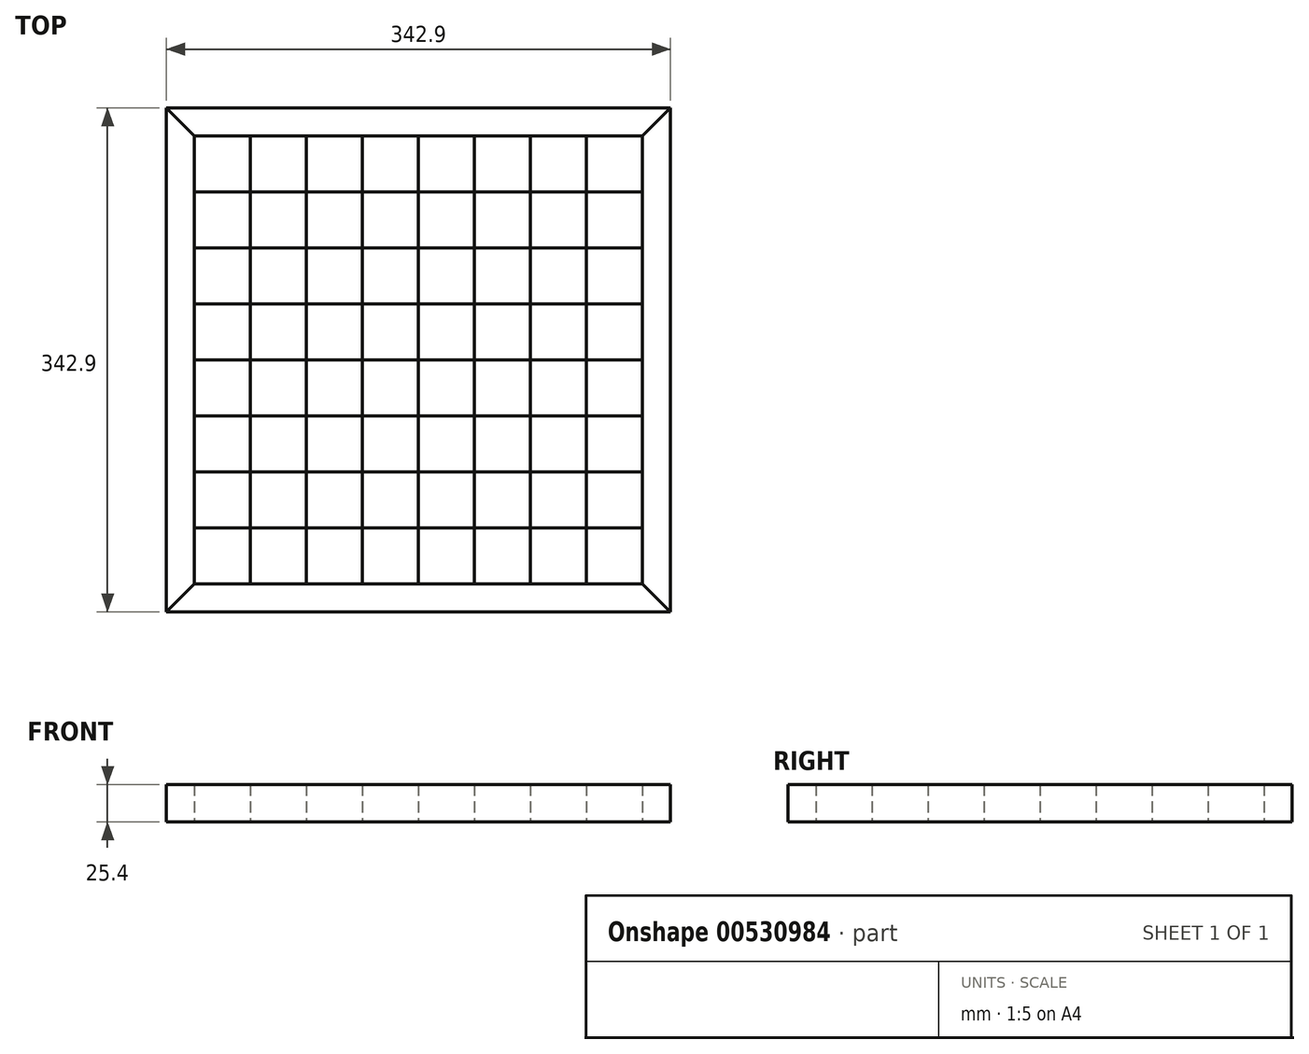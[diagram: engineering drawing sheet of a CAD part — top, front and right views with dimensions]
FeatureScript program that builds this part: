
annotation { "Feature Type Name" : "Feature", "Feature Type Description" : "" }
export const myFeature = defineFeature(function(context is Context, id is Id, definition is map)
    precondition{}
    {
        {
            var Q0;
            Q0=qCreatedBy(makeId("Top.planeOp"),FACE);
            var sketch = newSketch(context, id + "F0", { "sketchPlane" : qUnion([Q0])});
            skLineSegment(sketch, "E0.bottom", {"start": v(171.45, 171.45) * mm, "end": v(-171.45, 171.45) * mm});
            skLineSegment(sketch, "E0.top", {"start": v(171.45, -171.45) * mm, "end": v(-171.45, -171.45) * mm});
            skLineSegment(sketch, "E0.left", {"start": v(171.45, 171.45) * mm, "end": v(171.45, -171.45) * mm});
            skLineSegment(sketch, "E0.right", {"start": v(-171.45, 171.45) * mm, "end": v(-171.45, -171.45) * mm});
            skPoint(sketch, "E0.middle", {"position": v(0, 0) * mm});
            skLineSegment(sketch, "E1.bottom", {"start": v(152.4, 152.4) * mm, "end": v(-152.4, 152.4) * mm});
            skLineSegment(sketch, "E1.top", {"start": v(152.4, -152.4) * mm, "end": v(-152.4, -152.4) * mm});
            skLineSegment(sketch, "E1.left", {"start": v(152.4, 152.4) * mm, "end": v(152.4, -152.4) * mm});
            skLineSegment(sketch, "E1.right", {"start": v(-152.4, 152.4) * mm, "end": v(-152.4, -152.4) * mm});
            skLineSegment(sketch, "E2", {"start": v(152.4, 152.4) * mm, "end": v(171.45, 171.45) * mm});
            skLineSegment(sketch, "E3", {"start": v(152.4, -152.4) * mm, "end": v(171.45, -171.45) * mm});
            skLineSegment(sketch, "E4", {"start": v(-152.4, -152.4) * mm, "end": v(-171.45, -171.45) * mm});
            skLineSegment(sketch, "E5", {"start": v(-152.4, 152.4) * mm, "end": v(-171.45, 171.45) * mm});
            skLineSegment(sketch, "E6", {"start": v(-114.3, 152.4) * mm, "end": v(-114.3, -152.4) * mm});
            skLineSegment(sketch, "E7", {"start": v(-76.2, 152.4) * mm, "end": v(-76.2, -152.4) * mm});
            skLineSegment(sketch, "E8", {"start": v(-38.1, 152.4) * mm, "end": v(-38.1, -152.4) * mm});
            skLineSegment(sketch, "E9", {"start": v(0, -152.4) * mm, "end": v(0, 152.4) * mm});
            skLineSegment(sketch, "E10", {"start": v(38.1, 152.4) * mm, "end": v(38.1, -152.4) * mm});
            skLineSegment(sketch, "E11", {"start": v(76.2, 152.4) * mm, "end": v(76.2, -152.4) * mm});
            skLineSegment(sketch, "E12", {"start": v(114.3, 152.4) * mm, "end": v(114.3, -152.4) * mm});
            skLineSegment(sketch, "E13", {"start": v(-152.4, 0) * mm, "end": v(152.4, 0) * mm});
            skLineSegment(sketch, "E14", {"start": v(-152.4, 38.1) * mm, "end": v(152.4, 38.1) * mm});
            skLineSegment(sketch, "E15", {"start": v(-152.4, 76.2) * mm, "end": v(152.4, 76.2) * mm});
            skLineSegment(sketch, "E16", {"start": v(-152.4, 114.3) * mm, "end": v(152.4, 114.3) * mm});
            skLineSegment(sketch, "E17", {"start": v(-152.4, -38.1) * mm, "end": v(152.4, -38.1) * mm});
            skLineSegment(sketch, "E18", {"start": v(-152.4, -76.2) * mm, "end": v(152.4, -76.2) * mm});
            skLineSegment(sketch, "E19", {"start": v(-152.4, -114.3) * mm, "end": v(152.4, -114.3) * mm});
            skSolve(sketch);
        }
        {
            var Q0;
            Q0=makeQuery(id+"F0.imprint","IMPRINT",FACE,{"disambiguationData":[TD([[makeQuery(id+"F0.imprint","IMPRINT",EDGE,{"derivedFrom":sQuery(id+"F0.wireOp",EDGE,"E0.right")}),1.0]])]});
            extrude(context, id + "F1", {"entities" : qUnion([Q0]), "depth" : 25.4 * mm, "offsetDistance" : 25.4 * mm});
        }
        {
            var Q0;
            Q0=makeQuery(id+"F0.imprint","IMPRINT",FACE,{"disambiguationData":[TD([[makeQuery(id+"F0.imprint","IMPRINT",EDGE,{"derivedFrom":sQuery(id+"F0.wireOp",EDGE,"E0.bottom")}),1.0]])]});
            extrude(context, id + "F2", {"entities" : qUnion([Q0]), "depth" : 25.4 * mm, "offsetDistance" : 25.4 * mm});
        }
        {
            var Q0;
            Q0=makeQuery(id+"F0.imprint","IMPRINT",FACE,{"disambiguationData":[TD([[makeQuery(id+"F0.imprint","IMPRINT",EDGE,{"derivedFrom":sQuery(id+"F0.wireOp",EDGE,"E0.left")}),-1.0]])]});
            extrude(context, id + "F3", {"entities" : qUnion([Q0]), "depth" : 25.4 * mm, "offsetDistance" : 25.4 * mm});
        }
        {
            var Q0;
            Q0=makeQuery(id+"F0.imprint","IMPRINT",FACE,{"disambiguationData":[TD([[makeQuery(id+"F0.imprint","IMPRINT",EDGE,{"derivedFrom":sQuery(id+"F0.wireOp",EDGE,"E0.top")}),-1.0]])]});
            extrude(context, id + "F4", {"entities" : qUnion([Q0]), "depth" : 25.4 * mm, "offsetDistance" : 25.4 * mm});
        }
        {
            var Q0;
            {var subQ1=sQuery(id+"F0.wireOp",EDGE,"E1.bottom");var subQ3=sQuery(id+"F0.wireOp",EDGE,"E6");var subQ4=makeQuery(id+"F0.imprint","INTERSECT",VERTEX,{"derivedFrom":[subQ1,subQ3]});Q0=makeQuery(id+"F0.imprint","IMPRINT",FACE,{"disambiguationData":[TD([[makeQuery(id+"F0.imprint","IMPRINT",EDGE,{"disambiguationData":[TD([[subQ4,-1.0]])],"derivedFrom":subQ3}),-1.0]])]});}
            var Q1;
            {var subQ0=sQuery(id+"F0.wireOp",EDGE,"E16");var subQ1=sQuery(id+"F0.wireOp",EDGE,"E6");var subQ2=makeQuery(id+"F0.imprint","INTERSECT",VERTEX,{"derivedFrom":[subQ1,subQ0]});Q1=makeQuery(id+"F0.imprint","IMPRINT",FACE,{"disambiguationData":[TD([[makeQuery(id+"F0.imprint","IMPRINT",EDGE,{"disambiguationData":[TD([[subQ2,-1.0]])],"derivedFrom":subQ1}),1.0]])]});}
            var Q2;
            {var subQ0=sQuery(id+"F0.wireOp",EDGE,"E7");var subQ1=sQuery(id+"F0.wireOp",EDGE,"E1.bottom");var subQ2=makeQuery(id+"F0.imprint","INTERSECT",VERTEX,{"derivedFrom":[subQ1,subQ0]});Q2=makeQuery(id+"F0.imprint","IMPRINT",FACE,{"disambiguationData":[TD([[makeQuery(id+"F0.imprint","IMPRINT",EDGE,{"disambiguationData":[TD([[subQ2,1.0]])],"derivedFrom":subQ1}),1.0]])]});}
            var Q3;
            {var subQ0=sQuery(id+"F0.wireOp",EDGE,"E16");var subQ1=sQuery(id+"F0.wireOp",EDGE,"E8");var subQ2=makeQuery(id+"F0.imprint","INTERSECT",VERTEX,{"derivedFrom":[subQ1,subQ0]});Q3=makeQuery(id+"F0.imprint","IMPRINT",FACE,{"disambiguationData":[TD([[makeQuery(id+"F0.imprint","IMPRINT",EDGE,{"disambiguationData":[TD([[subQ2,-1.0]])],"derivedFrom":subQ1}),1.0]])]});}
            var Q4;
            {var subQ0=sQuery(id+"F0.wireOp",EDGE,"E9");var subQ1=sQuery(id+"F0.wireOp",EDGE,"E1.bottom");var subQ2=makeQuery(id+"F0.imprint","INTERSECT",VERTEX,{"derivedFrom":[subQ1,subQ0]});Q4=makeQuery(id+"F0.imprint","IMPRINT",FACE,{"disambiguationData":[TD([[makeQuery(id+"F0.imprint","IMPRINT",EDGE,{"disambiguationData":[TD([[subQ2,1.0]])],"derivedFrom":subQ1}),1.0]])]});}
            var Q5;
            {var subQ0=sQuery(id+"F0.wireOp",EDGE,"E16");var subQ1=sQuery(id+"F0.wireOp",EDGE,"E10");var subQ2=makeQuery(id+"F0.imprint","INTERSECT",VERTEX,{"derivedFrom":[subQ1,subQ0]});Q5=makeQuery(id+"F0.imprint","IMPRINT",FACE,{"disambiguationData":[TD([[makeQuery(id+"F0.imprint","IMPRINT",EDGE,{"disambiguationData":[TD([[subQ2,-1.0]])],"derivedFrom":subQ1}),1.0]])]});}
            var Q6;
            {var subQ0=sQuery(id+"F0.wireOp",EDGE,"E11");var subQ1=sQuery(id+"F0.wireOp",EDGE,"E1.bottom");var subQ2=makeQuery(id+"F0.imprint","INTERSECT",VERTEX,{"derivedFrom":[subQ1,subQ0]});Q6=makeQuery(id+"F0.imprint","IMPRINT",FACE,{"disambiguationData":[TD([[makeQuery(id+"F0.imprint","IMPRINT",EDGE,{"disambiguationData":[TD([[subQ2,1.0]])],"derivedFrom":subQ1}),1.0]])]});}
            var Q7;
            {var subQ0=sQuery(id+"F0.wireOp",EDGE,"E15");var subQ1=sQuery(id+"F0.wireOp",EDGE,"E1.left");var subQ2=makeQuery(id+"F0.imprint","INTERSECT",VERTEX,{"derivedFrom":[subQ1,subQ0]});Q7=makeQuery(id+"F0.imprint","IMPRINT",FACE,{"disambiguationData":[TD([[makeQuery(id+"F0.imprint","IMPRINT",EDGE,{"disambiguationData":[TD([[subQ2,1.0]])],"derivedFrom":subQ1}),-1.0]])]});}
            var Q8;
            {var subQ0=sQuery(id+"F0.wireOp",EDGE,"E15");var subQ1=sQuery(id+"F0.wireOp",EDGE,"E11");var subQ2=makeQuery(id+"F0.imprint","INTERSECT",VERTEX,{"derivedFrom":[subQ1,subQ0]});Q8=makeQuery(id+"F0.imprint","IMPRINT",FACE,{"disambiguationData":[TD([[makeQuery(id+"F0.imprint","IMPRINT",EDGE,{"disambiguationData":[TD([[subQ2,-1.0]])],"derivedFrom":subQ1}),1.0]])]});}
            var Q9;
            {var subQ0=sQuery(id+"F0.wireOp",EDGE,"E14");var subQ1=sQuery(id+"F0.wireOp",EDGE,"E10");var subQ2=makeQuery(id+"F0.imprint","INTERSECT",VERTEX,{"derivedFrom":[subQ1,subQ0]});Q9=makeQuery(id+"F0.imprint","IMPRINT",FACE,{"disambiguationData":[TD([[makeQuery(id+"F0.imprint","IMPRINT",EDGE,{"disambiguationData":[TD([[subQ2,-1.0]])],"derivedFrom":subQ1}),1.0]])]});}
            var Q10;
            {var subQ0=sQuery(id+"F0.wireOp",EDGE,"E13");var subQ1=sQuery(id+"F0.wireOp",EDGE,"E1.left");var subQ2=makeQuery(id+"F0.imprint","INTERSECT",VERTEX,{"derivedFrom":[subQ1,subQ0]});Q10=makeQuery(id+"F0.imprint","IMPRINT",FACE,{"disambiguationData":[TD([[makeQuery(id+"F0.imprint","IMPRINT",EDGE,{"disambiguationData":[TD([[subQ2,1.0]])],"derivedFrom":subQ1}),-1.0]])]});}
            var Q11;
            {var subQ0=sQuery(id+"F0.wireOp",EDGE,"E14");var subQ1=sQuery(id+"F0.wireOp",EDGE,"E9");var subQ2=makeQuery(id+"F0.imprint","INTERSECT",VERTEX,{"derivedFrom":[subQ1,subQ0]});Q11=makeQuery(id+"F0.imprint","IMPRINT",FACE,{"disambiguationData":[TD([[makeQuery(id+"F0.imprint","IMPRINT",EDGE,{"disambiguationData":[TD([[subQ2,-1.0]])],"derivedFrom":subQ1}),-1.0]])]});}
            var Q12;
            {var subQ0=sQuery(id+"F0.wireOp",EDGE,"E14");var subQ1=sQuery(id+"F0.wireOp",EDGE,"E8");var subQ2=makeQuery(id+"F0.imprint","INTERSECT",VERTEX,{"derivedFrom":[subQ1,subQ0]});Q12=makeQuery(id+"F0.imprint","IMPRINT",FACE,{"disambiguationData":[TD([[makeQuery(id+"F0.imprint","IMPRINT",EDGE,{"disambiguationData":[TD([[subQ2,-1.0]])],"derivedFrom":subQ1}),1.0]])]});}
            var Q13;
            {var subQ0=sQuery(id+"F0.wireOp",EDGE,"E15");var subQ1=sQuery(id+"F0.wireOp",EDGE,"E7");var subQ2=makeQuery(id+"F0.imprint","INTERSECT",VERTEX,{"derivedFrom":[subQ1,subQ0]});Q13=makeQuery(id+"F0.imprint","IMPRINT",FACE,{"disambiguationData":[TD([[makeQuery(id+"F0.imprint","IMPRINT",EDGE,{"disambiguationData":[TD([[subQ2,-1.0]])],"derivedFrom":subQ1}),1.0]])]});}
            var Q14;
            {var subQ0=sQuery(id+"F0.wireOp",EDGE,"E14");var subQ1=sQuery(id+"F0.wireOp",EDGE,"E6");var subQ2=makeQuery(id+"F0.imprint","INTERSECT",VERTEX,{"derivedFrom":[subQ1,subQ0]});Q14=makeQuery(id+"F0.imprint","IMPRINT",FACE,{"disambiguationData":[TD([[makeQuery(id+"F0.imprint","IMPRINT",EDGE,{"disambiguationData":[TD([[subQ2,-1.0]])],"derivedFrom":subQ1}),1.0]])]});}
            var Q15;
            {var subQ0=sQuery(id+"F0.wireOp",EDGE,"E14");var subQ1=sQuery(id+"F0.wireOp",EDGE,"E1.right");var subQ2=makeQuery(id+"F0.imprint","INTERSECT",VERTEX,{"derivedFrom":[subQ1,subQ0]});Q15=makeQuery(id+"F0.imprint","IMPRINT",FACE,{"disambiguationData":[TD([[makeQuery(id+"F0.imprint","IMPRINT",EDGE,{"disambiguationData":[TD([[subQ2,1.0]])],"derivedFrom":subQ1}),1.0]])]});}
            var Q16;
            {var subQ0=sQuery(id+"F0.wireOp",EDGE,"E13");var subQ1=sQuery(id+"F0.wireOp",EDGE,"E1.right");var subQ2=makeQuery(id+"F0.imprint","INTERSECT",VERTEX,{"derivedFrom":[subQ1,subQ0]});Q16=makeQuery(id+"F0.imprint","IMPRINT",FACE,{"disambiguationData":[TD([[makeQuery(id+"F0.imprint","IMPRINT",EDGE,{"disambiguationData":[TD([[subQ2,-1.0]])],"derivedFrom":subQ1}),1.0]])]});}
            var Q17;
            {var subQ0=sQuery(id+"F0.wireOp",EDGE,"E17");var subQ1=sQuery(id+"F0.wireOp",EDGE,"E6");var subQ2=makeQuery(id+"F0.imprint","INTERSECT",VERTEX,{"derivedFrom":[subQ1,subQ0]});Q17=makeQuery(id+"F0.imprint","IMPRINT",FACE,{"disambiguationData":[TD([[makeQuery(id+"F0.imprint","IMPRINT",EDGE,{"disambiguationData":[TD([[subQ2,-1.0]])],"derivedFrom":subQ1}),1.0]])]});}
            var Q18;
            {var subQ0=sQuery(id+"F0.wireOp",EDGE,"E13");var subQ1=sQuery(id+"F0.wireOp",EDGE,"E7");var subQ2=makeQuery(id+"F0.imprint","INTERSECT",VERTEX,{"derivedFrom":[subQ1,subQ0]});Q18=makeQuery(id+"F0.imprint","IMPRINT",FACE,{"disambiguationData":[TD([[makeQuery(id+"F0.imprint","IMPRINT",EDGE,{"disambiguationData":[TD([[subQ2,-1.0]])],"derivedFrom":subQ1}),1.0]])]});}
            var Q19;
            {var subQ0=sQuery(id+"F0.wireOp",EDGE,"E17");var subQ1=sQuery(id+"F0.wireOp",EDGE,"E8");var subQ2=makeQuery(id+"F0.imprint","INTERSECT",VERTEX,{"derivedFrom":[subQ1,subQ0]});Q19=makeQuery(id+"F0.imprint","IMPRINT",FACE,{"disambiguationData":[TD([[makeQuery(id+"F0.imprint","IMPRINT",EDGE,{"disambiguationData":[TD([[subQ2,-1.0]])],"derivedFrom":subQ1}),1.0]])]});}
            var Q20;
            {var subQ0=sQuery(id+"F0.wireOp",EDGE,"E17");var subQ1=sQuery(id+"F0.wireOp",EDGE,"E9");var subQ2=makeQuery(id+"F0.imprint","INTERSECT",VERTEX,{"derivedFrom":[subQ1,subQ0]});Q20=makeQuery(id+"F0.imprint","IMPRINT",FACE,{"disambiguationData":[TD([[makeQuery(id+"F0.imprint","IMPRINT",EDGE,{"disambiguationData":[TD([[subQ2,-1.0]])],"derivedFrom":subQ1}),-1.0]])]});}
            var Q21;
            {var subQ0=sQuery(id+"F0.wireOp",EDGE,"E17");var subQ1=sQuery(id+"F0.wireOp",EDGE,"E10");var subQ2=makeQuery(id+"F0.imprint","INTERSECT",VERTEX,{"derivedFrom":[subQ1,subQ0]});Q21=makeQuery(id+"F0.imprint","IMPRINT",FACE,{"disambiguationData":[TD([[makeQuery(id+"F0.imprint","IMPRINT",EDGE,{"disambiguationData":[TD([[subQ2,-1.0]])],"derivedFrom":subQ1}),1.0]])]});}
            var Q22;
            {var subQ0=sQuery(id+"F0.wireOp",EDGE,"E13");var subQ1=sQuery(id+"F0.wireOp",EDGE,"E11");var subQ2=makeQuery(id+"F0.imprint","INTERSECT",VERTEX,{"derivedFrom":[subQ1,subQ0]});Q22=makeQuery(id+"F0.imprint","IMPRINT",FACE,{"disambiguationData":[TD([[makeQuery(id+"F0.imprint","IMPRINT",EDGE,{"disambiguationData":[TD([[subQ2,-1.0]])],"derivedFrom":subQ1}),1.0]])]});}
            var Q23;
            {var subQ0=sQuery(id+"F0.wireOp",EDGE,"E17");var subQ1=sQuery(id+"F0.wireOp",EDGE,"E1.left");var subQ2=makeQuery(id+"F0.imprint","INTERSECT",VERTEX,{"derivedFrom":[subQ1,subQ0]});Q23=makeQuery(id+"F0.imprint","IMPRINT",FACE,{"disambiguationData":[TD([[makeQuery(id+"F0.imprint","IMPRINT",EDGE,{"disambiguationData":[TD([[subQ2,-1.0]])],"derivedFrom":subQ1}),-1.0]])]});}
            var Q24;
            {var subQ0=sQuery(id+"F0.wireOp",EDGE,"E18");var subQ1=sQuery(id+"F0.wireOp",EDGE,"E11");var subQ2=makeQuery(id+"F0.imprint","INTERSECT",VERTEX,{"derivedFrom":[subQ1,subQ0]});Q24=makeQuery(id+"F0.imprint","IMPRINT",FACE,{"disambiguationData":[TD([[makeQuery(id+"F0.imprint","IMPRINT",EDGE,{"disambiguationData":[TD([[subQ2,-1.0]])],"derivedFrom":subQ1}),1.0]])]});}
            var Q25;
            {var subQ0=sQuery(id+"F0.wireOp",EDGE,"E19");var subQ1=sQuery(id+"F0.wireOp",EDGE,"E9");var subQ2=makeQuery(id+"F0.imprint","INTERSECT",VERTEX,{"derivedFrom":[subQ1,subQ0]});Q25=makeQuery(id+"F0.imprint","IMPRINT",FACE,{"disambiguationData":[TD([[makeQuery(id+"F0.imprint","IMPRINT",EDGE,{"disambiguationData":[TD([[subQ2,-1.0]])],"derivedFrom":subQ1}),-1.0]])]});}
            var Q26;
            {var subQ0=sQuery(id+"F0.wireOp",EDGE,"E18");var subQ1=sQuery(id+"F0.wireOp",EDGE,"E7");var subQ2=makeQuery(id+"F0.imprint","INTERSECT",VERTEX,{"derivedFrom":[subQ1,subQ0]});Q26=makeQuery(id+"F0.imprint","IMPRINT",FACE,{"disambiguationData":[TD([[makeQuery(id+"F0.imprint","IMPRINT",EDGE,{"disambiguationData":[TD([[subQ2,-1.0]])],"derivedFrom":subQ1}),1.0]])]});}
            var Q27;
            {var subQ0=sQuery(id+"F0.wireOp",EDGE,"E18");var subQ1=sQuery(id+"F0.wireOp",EDGE,"E1.right");var subQ2=makeQuery(id+"F0.imprint","INTERSECT",VERTEX,{"derivedFrom":[subQ1,subQ0]});Q27=makeQuery(id+"F0.imprint","IMPRINT",FACE,{"disambiguationData":[TD([[makeQuery(id+"F0.imprint","IMPRINT",EDGE,{"disambiguationData":[TD([[subQ2,-1.0]])],"derivedFrom":subQ1}),1.0]])]});}
            var Q28;
            {var subQ0=sQuery(id+"F0.wireOp",EDGE,"E6");var subQ1=sQuery(id+"F0.wireOp",EDGE,"E1.top");var subQ2=makeQuery(id+"F0.imprint","INTERSECT",VERTEX,{"derivedFrom":[subQ1,subQ0]});Q28=makeQuery(id+"F0.imprint","IMPRINT",FACE,{"disambiguationData":[TD([[makeQuery(id+"F0.imprint","IMPRINT",EDGE,{"disambiguationData":[TD([[subQ2,1.0]])],"derivedFrom":subQ1}),-1.0]])]});}
            var Q29;
            {var subQ0=sQuery(id+"F0.wireOp",EDGE,"E8");var subQ1=sQuery(id+"F0.wireOp",EDGE,"E1.top");var subQ2=makeQuery(id+"F0.imprint","INTERSECT",VERTEX,{"derivedFrom":[subQ1,subQ0]});Q29=makeQuery(id+"F0.imprint","IMPRINT",FACE,{"disambiguationData":[TD([[makeQuery(id+"F0.imprint","IMPRINT",EDGE,{"disambiguationData":[TD([[subQ2,1.0]])],"derivedFrom":subQ1}),-1.0]])]});}
            var Q30;
            {var subQ0=sQuery(id+"F0.wireOp",EDGE,"E10");var subQ1=sQuery(id+"F0.wireOp",EDGE,"E1.top");var subQ2=makeQuery(id+"F0.imprint","INTERSECT",VERTEX,{"derivedFrom":[subQ1,subQ0]});Q30=makeQuery(id+"F0.imprint","IMPRINT",FACE,{"disambiguationData":[TD([[makeQuery(id+"F0.imprint","IMPRINT",EDGE,{"disambiguationData":[TD([[subQ2,1.0]])],"derivedFrom":subQ1}),-1.0]])]});}
            var Q31;
            {var subQ1=sQuery(id+"F0.wireOp",EDGE,"E1.top");var subQ3=sQuery(id+"F0.wireOp",EDGE,"E12");var subQ4=makeQuery(id+"F0.imprint","INTERSECT",VERTEX,{"derivedFrom":[subQ1,subQ3]});Q31=makeQuery(id+"F0.imprint","IMPRINT",FACE,{"disambiguationData":[TD([[makeQuery(id+"F0.imprint","IMPRINT",EDGE,{"disambiguationData":[TD([[subQ4,1.0]])],"derivedFrom":subQ3}),1.0]])]});}
            extrude(context, id + "F5", {"entities" : qUnion([Q0, Q1, Q2, Q3, Q4, Q5, Q6, Q7, Q8, Q9, Q10, Q11, Q12, Q13, Q14, Q15, Q16, Q17, Q18, Q19, Q20, Q21, Q22, Q23, Q24, Q25, Q26, Q27, Q28, Q29, Q30, Q31]), "depth" : 25.4 * mm, "offsetDistance" : 25.4 * mm});
        }
        {
            var Q0;
            {var subQ0=sQuery(id+"F0.wireOp",EDGE,"E6");var subQ1=sQuery(id+"F0.wireOp",EDGE,"E1.bottom");var subQ2=makeQuery(id+"F0.imprint","INTERSECT",VERTEX,{"derivedFrom":[subQ1,subQ0]});Q0=makeQuery(id+"F0.imprint","IMPRINT",FACE,{"disambiguationData":[TD([[makeQuery(id+"F0.imprint","IMPRINT",EDGE,{"disambiguationData":[TD([[subQ2,1.0]])],"derivedFrom":subQ1}),1.0]])]});}
            var Q1;
            {var subQ0=sQuery(id+"F0.wireOp",EDGE,"E16");var subQ1=sQuery(id+"F0.wireOp",EDGE,"E7");var subQ2=makeQuery(id+"F0.imprint","INTERSECT",VERTEX,{"derivedFrom":[subQ1,subQ0]});Q1=makeQuery(id+"F0.imprint","IMPRINT",FACE,{"disambiguationData":[TD([[makeQuery(id+"F0.imprint","IMPRINT",EDGE,{"disambiguationData":[TD([[subQ2,-1.0]])],"derivedFrom":subQ1}),1.0]])]});}
            var Q2;
            {var subQ0=sQuery(id+"F0.wireOp",EDGE,"E8");var subQ1=sQuery(id+"F0.wireOp",EDGE,"E1.bottom");var subQ2=makeQuery(id+"F0.imprint","INTERSECT",VERTEX,{"derivedFrom":[subQ1,subQ0]});Q2=makeQuery(id+"F0.imprint","IMPRINT",FACE,{"disambiguationData":[TD([[makeQuery(id+"F0.imprint","IMPRINT",EDGE,{"disambiguationData":[TD([[subQ2,1.0]])],"derivedFrom":subQ1}),1.0]])]});}
            var Q3;
            {var subQ0=sQuery(id+"F0.wireOp",EDGE,"E10");var subQ1=sQuery(id+"F0.wireOp",EDGE,"E1.bottom");var subQ2=makeQuery(id+"F0.imprint","INTERSECT",VERTEX,{"derivedFrom":[subQ1,subQ0]});Q3=makeQuery(id+"F0.imprint","IMPRINT",FACE,{"disambiguationData":[TD([[makeQuery(id+"F0.imprint","IMPRINT",EDGE,{"disambiguationData":[TD([[subQ2,1.0]])],"derivedFrom":subQ1}),1.0]])]});}
            var Q4;
            {var subQ0=sQuery(id+"F0.wireOp",EDGE,"E15");var subQ1=sQuery(id+"F0.wireOp",EDGE,"E9");var subQ2=makeQuery(id+"F0.imprint","INTERSECT",VERTEX,{"derivedFrom":[subQ1,subQ0]});Q4=makeQuery(id+"F0.imprint","IMPRINT",FACE,{"disambiguationData":[TD([[makeQuery(id+"F0.imprint","IMPRINT",EDGE,{"disambiguationData":[TD([[subQ2,-1.0]])],"derivedFrom":subQ1}),-1.0]])]});}
            var Q5;
            {var subQ0=sQuery(id+"F0.wireOp",EDGE,"E16");var subQ1=sQuery(id+"F0.wireOp",EDGE,"E11");var subQ2=makeQuery(id+"F0.imprint","INTERSECT",VERTEX,{"derivedFrom":[subQ1,subQ0]});Q5=makeQuery(id+"F0.imprint","IMPRINT",FACE,{"disambiguationData":[TD([[makeQuery(id+"F0.imprint","IMPRINT",EDGE,{"disambiguationData":[TD([[subQ2,-1.0]])],"derivedFrom":subQ1}),1.0]])]});}
            var Q6;
            {var subQ1=sQuery(id+"F0.wireOp",EDGE,"E1.bottom");var subQ3=sQuery(id+"F0.wireOp",EDGE,"E12");var subQ4=makeQuery(id+"F0.imprint","INTERSECT",VERTEX,{"derivedFrom":[subQ1,subQ3]});Q6=makeQuery(id+"F0.imprint","IMPRINT",FACE,{"disambiguationData":[TD([[makeQuery(id+"F0.imprint","IMPRINT",EDGE,{"disambiguationData":[TD([[subQ4,-1.0]])],"derivedFrom":subQ3}),1.0]])]});}
            var Q7;
            {var subQ0=sQuery(id+"F0.wireOp",EDGE,"E15");var subQ1=sQuery(id+"F0.wireOp",EDGE,"E1.right");var subQ2=makeQuery(id+"F0.imprint","INTERSECT",VERTEX,{"derivedFrom":[subQ1,subQ0]});Q7=makeQuery(id+"F0.imprint","IMPRINT",FACE,{"disambiguationData":[TD([[makeQuery(id+"F0.imprint","IMPRINT",EDGE,{"disambiguationData":[TD([[subQ2,1.0]])],"derivedFrom":subQ1}),1.0]])]});}
            var Q8;
            {var subQ0=sQuery(id+"F0.wireOp",EDGE,"E15");var subQ1=sQuery(id+"F0.wireOp",EDGE,"E6");var subQ2=makeQuery(id+"F0.imprint","INTERSECT",VERTEX,{"derivedFrom":[subQ1,subQ0]});Q8=makeQuery(id+"F0.imprint","IMPRINT",FACE,{"disambiguationData":[TD([[makeQuery(id+"F0.imprint","IMPRINT",EDGE,{"disambiguationData":[TD([[subQ2,-1.0]])],"derivedFrom":subQ1}),1.0]])]});}
            var Q9;
            {var subQ0=sQuery(id+"F0.wireOp",EDGE,"E15");var subQ1=sQuery(id+"F0.wireOp",EDGE,"E8");var subQ2=makeQuery(id+"F0.imprint","INTERSECT",VERTEX,{"derivedFrom":[subQ1,subQ0]});Q9=makeQuery(id+"F0.imprint","IMPRINT",FACE,{"disambiguationData":[TD([[makeQuery(id+"F0.imprint","IMPRINT",EDGE,{"disambiguationData":[TD([[subQ2,-1.0]])],"derivedFrom":subQ1}),1.0]])]});}
            var Q10;
            {var subQ0=sQuery(id+"F0.wireOp",EDGE,"E15");var subQ1=sQuery(id+"F0.wireOp",EDGE,"E10");var subQ2=makeQuery(id+"F0.imprint","INTERSECT",VERTEX,{"derivedFrom":[subQ1,subQ0]});Q10=makeQuery(id+"F0.imprint","IMPRINT",FACE,{"disambiguationData":[TD([[makeQuery(id+"F0.imprint","IMPRINT",EDGE,{"disambiguationData":[TD([[subQ2,-1.0]])],"derivedFrom":subQ1}),1.0]])]});}
            var Q11;
            {var subQ0=sQuery(id+"F0.wireOp",EDGE,"E14");var subQ1=sQuery(id+"F0.wireOp",EDGE,"E1.left");var subQ2=makeQuery(id+"F0.imprint","INTERSECT",VERTEX,{"derivedFrom":[subQ1,subQ0]});Q11=makeQuery(id+"F0.imprint","IMPRINT",FACE,{"disambiguationData":[TD([[makeQuery(id+"F0.imprint","IMPRINT",EDGE,{"disambiguationData":[TD([[subQ2,1.0]])],"derivedFrom":subQ1}),-1.0]])]});}
            var Q12;
            {var subQ0=sQuery(id+"F0.wireOp",EDGE,"E14");var subQ1=sQuery(id+"F0.wireOp",EDGE,"E11");var subQ2=makeQuery(id+"F0.imprint","INTERSECT",VERTEX,{"derivedFrom":[subQ1,subQ0]});Q12=makeQuery(id+"F0.imprint","IMPRINT",FACE,{"disambiguationData":[TD([[makeQuery(id+"F0.imprint","IMPRINT",EDGE,{"disambiguationData":[TD([[subQ2,-1.0]])],"derivedFrom":subQ1}),1.0]])]});}
            var Q13;
            {var subQ0=sQuery(id+"F0.wireOp",EDGE,"E13");var subQ1=sQuery(id+"F0.wireOp",EDGE,"E1.left");var subQ2=makeQuery(id+"F0.imprint","INTERSECT",VERTEX,{"derivedFrom":[subQ1,subQ0]});Q13=makeQuery(id+"F0.imprint","IMPRINT",FACE,{"disambiguationData":[TD([[makeQuery(id+"F0.imprint","IMPRINT",EDGE,{"disambiguationData":[TD([[subQ2,-1.0]])],"derivedFrom":subQ1}),-1.0]])]});}
            var Q14;
            {var subQ0=sQuery(id+"F0.wireOp",EDGE,"E13");var subQ1=sQuery(id+"F0.wireOp",EDGE,"E10");var subQ2=makeQuery(id+"F0.imprint","INTERSECT",VERTEX,{"derivedFrom":[subQ1,subQ0]});Q14=makeQuery(id+"F0.imprint","IMPRINT",FACE,{"disambiguationData":[TD([[makeQuery(id+"F0.imprint","IMPRINT",EDGE,{"disambiguationData":[TD([[subQ2,-1.0]])],"derivedFrom":subQ1}),1.0]])]});}
            var Q15;
            {var subQ0=sQuery(id+"F0.wireOp",EDGE,"E13");var subQ1=sQuery(id+"F0.wireOp",EDGE,"E9");var subQ2=makeQuery(id+"F0.imprint","INTERSECT",VERTEX,{"derivedFrom":[subQ1,subQ0]});Q15=makeQuery(id+"F0.imprint","IMPRINT",FACE,{"disambiguationData":[TD([[makeQuery(id+"F0.imprint","IMPRINT",EDGE,{"disambiguationData":[TD([[subQ2,-1.0]])],"derivedFrom":subQ1}),-1.0]])]});}
            var Q16;
            {var subQ0=sQuery(id+"F0.wireOp",EDGE,"E13");var subQ1=sQuery(id+"F0.wireOp",EDGE,"E8");var subQ2=makeQuery(id+"F0.imprint","INTERSECT",VERTEX,{"derivedFrom":[subQ1,subQ0]});Q16=makeQuery(id+"F0.imprint","IMPRINT",FACE,{"disambiguationData":[TD([[makeQuery(id+"F0.imprint","IMPRINT",EDGE,{"disambiguationData":[TD([[subQ2,-1.0]])],"derivedFrom":subQ1}),1.0]])]});}
            var Q17;
            {var subQ0=sQuery(id+"F0.wireOp",EDGE,"E14");var subQ1=sQuery(id+"F0.wireOp",EDGE,"E7");var subQ2=makeQuery(id+"F0.imprint","INTERSECT",VERTEX,{"derivedFrom":[subQ1,subQ0]});Q17=makeQuery(id+"F0.imprint","IMPRINT",FACE,{"disambiguationData":[TD([[makeQuery(id+"F0.imprint","IMPRINT",EDGE,{"disambiguationData":[TD([[subQ2,-1.0]])],"derivedFrom":subQ1}),1.0]])]});}
            var Q18;
            {var subQ0=sQuery(id+"F0.wireOp",EDGE,"E13");var subQ1=sQuery(id+"F0.wireOp",EDGE,"E6");var subQ2=makeQuery(id+"F0.imprint","INTERSECT",VERTEX,{"derivedFrom":[subQ1,subQ0]});Q18=makeQuery(id+"F0.imprint","IMPRINT",FACE,{"disambiguationData":[TD([[makeQuery(id+"F0.imprint","IMPRINT",EDGE,{"disambiguationData":[TD([[subQ2,-1.0]])],"derivedFrom":subQ1}),1.0]])]});}
            var Q19;
            {var subQ0=sQuery(id+"F0.wireOp",EDGE,"E13");var subQ1=sQuery(id+"F0.wireOp",EDGE,"E1.right");var subQ2=makeQuery(id+"F0.imprint","INTERSECT",VERTEX,{"derivedFrom":[subQ1,subQ0]});Q19=makeQuery(id+"F0.imprint","IMPRINT",FACE,{"disambiguationData":[TD([[makeQuery(id+"F0.imprint","IMPRINT",EDGE,{"disambiguationData":[TD([[subQ2,1.0]])],"derivedFrom":subQ1}),1.0]])]});}
            var Q20;
            {var subQ0=sQuery(id+"F0.wireOp",EDGE,"E17");var subQ1=sQuery(id+"F0.wireOp",EDGE,"E1.right");var subQ2=makeQuery(id+"F0.imprint","INTERSECT",VERTEX,{"derivedFrom":[subQ1,subQ0]});Q20=makeQuery(id+"F0.imprint","IMPRINT",FACE,{"disambiguationData":[TD([[makeQuery(id+"F0.imprint","IMPRINT",EDGE,{"disambiguationData":[TD([[subQ2,-1.0]])],"derivedFrom":subQ1}),1.0]])]});}
            var Q21;
            {var subQ0=sQuery(id+"F0.wireOp",EDGE,"E18");var subQ1=sQuery(id+"F0.wireOp",EDGE,"E6");var subQ2=makeQuery(id+"F0.imprint","INTERSECT",VERTEX,{"derivedFrom":[subQ1,subQ0]});Q21=makeQuery(id+"F0.imprint","IMPRINT",FACE,{"disambiguationData":[TD([[makeQuery(id+"F0.imprint","IMPRINT",EDGE,{"disambiguationData":[TD([[subQ2,-1.0]])],"derivedFrom":subQ1}),1.0]])]});}
            var Q22;
            {var subQ1=sQuery(id+"F0.wireOp",EDGE,"E1.top");var subQ3=sQuery(id+"F0.wireOp",EDGE,"E6");var subQ4=makeQuery(id+"F0.imprint","INTERSECT",VERTEX,{"derivedFrom":[subQ1,subQ3]});Q22=makeQuery(id+"F0.imprint","IMPRINT",FACE,{"disambiguationData":[TD([[makeQuery(id+"F0.imprint","IMPRINT",EDGE,{"disambiguationData":[TD([[subQ4,1.0]])],"derivedFrom":subQ3}),-1.0]])]});}
            var Q23;
            {var subQ0=sQuery(id+"F0.wireOp",EDGE,"E7");var subQ1=sQuery(id+"F0.wireOp",EDGE,"E1.top");var subQ2=makeQuery(id+"F0.imprint","INTERSECT",VERTEX,{"derivedFrom":[subQ1,subQ0]});Q23=makeQuery(id+"F0.imprint","IMPRINT",FACE,{"disambiguationData":[TD([[makeQuery(id+"F0.imprint","IMPRINT",EDGE,{"disambiguationData":[TD([[subQ2,1.0]])],"derivedFrom":subQ1}),-1.0]])]});}
            var Q24;
            {var subQ0=sQuery(id+"F0.wireOp",EDGE,"E17");var subQ1=sQuery(id+"F0.wireOp",EDGE,"E7");var subQ2=makeQuery(id+"F0.imprint","INTERSECT",VERTEX,{"derivedFrom":[subQ1,subQ0]});Q24=makeQuery(id+"F0.imprint","IMPRINT",FACE,{"disambiguationData":[TD([[makeQuery(id+"F0.imprint","IMPRINT",EDGE,{"disambiguationData":[TD([[subQ2,-1.0]])],"derivedFrom":subQ1}),1.0]])]});}
            var Q25;
            {var subQ0=sQuery(id+"F0.wireOp",EDGE,"E18");var subQ1=sQuery(id+"F0.wireOp",EDGE,"E8");var subQ2=makeQuery(id+"F0.imprint","INTERSECT",VERTEX,{"derivedFrom":[subQ1,subQ0]});Q25=makeQuery(id+"F0.imprint","IMPRINT",FACE,{"disambiguationData":[TD([[makeQuery(id+"F0.imprint","IMPRINT",EDGE,{"disambiguationData":[TD([[subQ2,-1.0]])],"derivedFrom":subQ1}),1.0]])]});}
            var Q26;
            {var subQ0=sQuery(id+"F0.wireOp",EDGE,"E18");var subQ1=sQuery(id+"F0.wireOp",EDGE,"E9");var subQ2=makeQuery(id+"F0.imprint","INTERSECT",VERTEX,{"derivedFrom":[subQ1,subQ0]});Q26=makeQuery(id+"F0.imprint","IMPRINT",FACE,{"disambiguationData":[TD([[makeQuery(id+"F0.imprint","IMPRINT",EDGE,{"disambiguationData":[TD([[subQ2,-1.0]])],"derivedFrom":subQ1}),-1.0]])]});}
            var Q27;
            {var subQ0=sQuery(id+"F0.wireOp",EDGE,"E9");var subQ1=sQuery(id+"F0.wireOp",EDGE,"E1.top");var subQ2=makeQuery(id+"F0.imprint","INTERSECT",VERTEX,{"derivedFrom":[subQ1,subQ0]});Q27=makeQuery(id+"F0.imprint","IMPRINT",FACE,{"disambiguationData":[TD([[makeQuery(id+"F0.imprint","IMPRINT",EDGE,{"disambiguationData":[TD([[subQ2,1.0]])],"derivedFrom":subQ1}),-1.0]])]});}
            var Q28;
            {var subQ0=sQuery(id+"F0.wireOp",EDGE,"E18");var subQ1=sQuery(id+"F0.wireOp",EDGE,"E10");var subQ2=makeQuery(id+"F0.imprint","INTERSECT",VERTEX,{"derivedFrom":[subQ1,subQ0]});Q28=makeQuery(id+"F0.imprint","IMPRINT",FACE,{"disambiguationData":[TD([[makeQuery(id+"F0.imprint","IMPRINT",EDGE,{"disambiguationData":[TD([[subQ2,-1.0]])],"derivedFrom":subQ1}),1.0]])]});}
            var Q29;
            {var subQ0=sQuery(id+"F0.wireOp",EDGE,"E11");var subQ1=sQuery(id+"F0.wireOp",EDGE,"E1.top");var subQ2=makeQuery(id+"F0.imprint","INTERSECT",VERTEX,{"derivedFrom":[subQ1,subQ0]});Q29=makeQuery(id+"F0.imprint","IMPRINT",FACE,{"disambiguationData":[TD([[makeQuery(id+"F0.imprint","IMPRINT",EDGE,{"disambiguationData":[TD([[subQ2,1.0]])],"derivedFrom":subQ1}),-1.0]])]});}
            var Q30;
            {var subQ0=sQuery(id+"F0.wireOp",EDGE,"E18");var subQ1=sQuery(id+"F0.wireOp",EDGE,"E1.left");var subQ2=makeQuery(id+"F0.imprint","INTERSECT",VERTEX,{"derivedFrom":[subQ1,subQ0]});Q30=makeQuery(id+"F0.imprint","IMPRINT",FACE,{"disambiguationData":[TD([[makeQuery(id+"F0.imprint","IMPRINT",EDGE,{"disambiguationData":[TD([[subQ2,-1.0]])],"derivedFrom":subQ1}),-1.0]])]});}
            var Q31;
            {var subQ0=sQuery(id+"F0.wireOp",EDGE,"E17");var subQ1=sQuery(id+"F0.wireOp",EDGE,"E11");var subQ2=makeQuery(id+"F0.imprint","INTERSECT",VERTEX,{"derivedFrom":[subQ1,subQ0]});Q31=makeQuery(id+"F0.imprint","IMPRINT",FACE,{"disambiguationData":[TD([[makeQuery(id+"F0.imprint","IMPRINT",EDGE,{"disambiguationData":[TD([[subQ2,-1.0]])],"derivedFrom":subQ1}),1.0]])]});}
            extrude(context, id + "F6", {"entities" : qUnion([Q0, Q1, Q2, Q3, Q4, Q5, Q6, Q7, Q8, Q9, Q10, Q11, Q12, Q13, Q14, Q15, Q16, Q17, Q18, Q19, Q20, Q21, Q22, Q23, Q24, Q25, Q26, Q27, Q28, Q29, Q30, Q31]), "depth" : 25.4 * mm, "offsetDistance" : 25.4 * mm});
        }
    });
